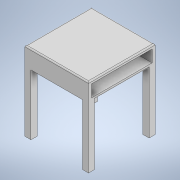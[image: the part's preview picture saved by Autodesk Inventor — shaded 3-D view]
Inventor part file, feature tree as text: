
AUTODESK INVENTOR PART (.ipt)
format: ipt  version: 2021 (Build 250183000, 183)  size: 149,504 bytes
history: native  units: in
note: dims shown in document units (in); Inventor stores cm internally (conversion verified against a paired STEP export)
features: extrude x3, sketch x3, other x1, fillet x1
ambient origin geometry x8: Origin, YZ Plane, XZ Plane, XY Plane, X Axis, Y Axis, Z Axis, Center Point
bodies: Body1 (feature_tree)
feature tree (8):
  other  "Sólido1"
  extrude  "Extrusión1"  Depth=4.3307in
  extrude  "Extrusión2"  Depth=4.3307in
  extrude  "Extrusión3"  Depth=0.1969in
  fillet  "Empalme1"  Radius=0.1969in
  sketch  "Boceto1"  dims[d0=2.1654in d1=4.3307in]
  sketch  "Boceto2"  dims[d2=4.1339in d3=4.3307in]
  sketch  "Boceto3"  dims[d4=1.1811in d5=0.0in d6=0.1969in d7=0.1969in d9=4.3307in d10=0.1969in d11=0.1969in d12=3.937in d13=0.0in d14=0.3937in d15=0.3937in d16=0.3937in d17=0.3937in d18=3.937in d19=0.0in d20=0.0787in]
